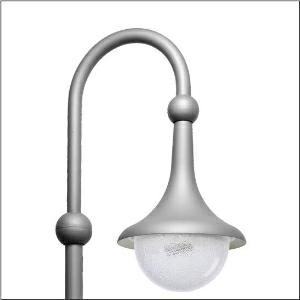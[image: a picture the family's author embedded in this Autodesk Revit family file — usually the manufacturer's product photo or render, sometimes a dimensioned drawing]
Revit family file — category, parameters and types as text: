
# Revit family: grosse_glocke___st1_2a_5xa1563e1b208_1d7c
name_source: partatom
category: Lighting Fixtures
units: mm (PartAtom-declared; Revit-internal decimal feet)

## family parameters
Cut with Voids When Loaded = No
Host = Face
Light Source = No
Part Type = Normal
Room Calculation Point = No
Round Connector Dimension = Use Diameter
Shared = No

## types (1)
- --- (1 x LED, 3210 lm, 23.4 W, 3000K)
    Apparent Load = 23 VA
    CIE Flux Codes = 29 66 94 99 100
    Color Rendering = 70
    Color Temperature = 3000K
    Default Elevation = 1800 mm
    Description = Large Bell, mast luminaire, primary light control with 3 zone facetted reflector, of plastic, silver coated, primary optical cover: enclosure, of PMMA, transparent structured, light distribution: ST1.2a, light emission: direct distribution, primary light characteristic: asymmetric, installation type: suspended mounting, LED, High Power LED, rated luminous flux: 3.210lm, luminous efficacy: 137lm/W, light colour: 730, colour temperature: 3000K, control gear: ECG Plus, control: flexible luminous flux parameterisation, time-dependent luminous flux control, constant luminous flux control, digital communication interface, power reduction, electronic power reduction, mains connection: 230..240V, AC, 50/60Hz, start of lifetime: 23W, end of service life: 24W, reduction: 12W, luminaire housing, bell-shaped, of glass-fibre reinforced polyester, coated, Siteco® metallic grey (DB 702S), please order curved mast extension separately, diameter: 530mm, height: 695mm, protection rating (complete): IP54, insulation class (complete): insulation class II (safety insulation), certification: CE, ENEC, VDE, impact resistance: IK08, standard-compliant lighting for roads and squares, packaging unit: 1 piece

Light Distribution: ST1.2a
    Height = 695 mm
    Lamp = 1 x LED
    Lamp Light Flux = 3210 lm
    Lamp Power = 23.4 W
    Lamp count = 1
    Length = 530 mm
    Luminous efficacy = 137 lm/W
    Manufacturer = Siteco
    ModVariant = No
    Model = 5XA1563E1B208
    Number of Poles = 1
    OnlyDefault = Yes
    Power Factor = 1
    Product Name = Große Glocke | ST1.2a
    Product group = mast luminaire | pylon annexe
    ProductGroupID = 6201
    Protection Class = Protection class II
    Protection Degree = IP 54
    RLX_Detail_Level = 1
    RLX_Emergency_Light_Flux = 0 lm
    RLX_Emergency_Type = 0
    RLX_Emergency_Type_DB = No
    RlxData = <blob elided: 54993 chars, md5=98bbab2e>
    Socket = socket
    Standby Power = 0 W
    System Light Flux = 3210 lm
    System Power = 23 W
    Type Comments = factory setting: luminous flux: 100 % | dim-lin: 254 | 460 mA
    Type Image = l_1284387.jpg
    URL = http://relux.com
    VarID = @adj_109101
    Voltage = 0 V
    Weight = 0.00 kg
    Width = 0 mm  [stored 0 ft]

note: [stored X ft] marks values corroborated as IEEE doubles in the binary element streams (Revit-internal decimal feet)

## geometry (parser evidence)
native form markers: Blend x4, Sweep x11
no freeform markers — native parametric forms only
